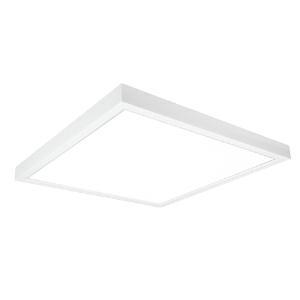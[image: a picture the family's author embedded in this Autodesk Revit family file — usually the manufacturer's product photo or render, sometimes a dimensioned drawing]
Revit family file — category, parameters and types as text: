
# Revit family: 3f_filippi_-_p_250_luce_diffusa_op_3f_filippi_-_10053_-_p_250_28w_led_dali_op_596x596
name_source: partatom
category: Lighting Fixtures
units: mm (PartAtom-declared; Revit-internal decimal feet)

## family parameters
Cut with Voids When Loaded = No
Host = Face
Light Source = No
Part Type = Normal
Room Calculation Point = No
Round Connector Dimension = Use Diameter
Shared = No

## types (1)
- 3F Filippi - P 250 Luce Diffusa OP (1 x LED, 4083 lm, 31 W, 4000 K)
    Apparent Load = 31 VA
    Approval mark = ENEC
    CIE Flux Codes = 48 80 96 100 100
    Color Rendering = 80
    Color Temperature = 4000 K
    Control Gear = Electronic transformer
    Default Elevation = 1800 mm
    Description = ILLUMINOTECHNICAL
Luminous efficiency 100% (DLOR 100%, ULOR 0%).
Initial luminous flux of the luminaire 4083 lm.
Direct distribution with soft, diffused and controlled light.
Installation Interdistance Transv.D = 1.24 x hu - Long.D = 1.21 x hu.
Tabular UGR (CIE 117 - 4H-8H; S=0.25H; 70/50/20): RUG 21.6 - 21.6.
Beam angle: 111° - 109°.
Luminous efficacy 132 lm/W.
Lifetime (L93/B10): 30000 h. (tq+25°C)
Lifetime (L90/B10): 50000 h. (tq+25°C)
Lifetime (L85/B10): 80000 h. (tq+25°C)
Lifetime (L80/B10): 100000 h. (tq+25°C)
Sudden decreased luminous flux after 50000 hours: 0% (C0).
Photobiological safety in compliance with IEC/TR 62778: RG0 risk exempt, (IEC 62471).
In compliance with IEC/EN 62722-2-1 - IEC/EN 62717 standards.

SOURCE
Squared LED module 28W/840.
Energy efficiency class (UE 2019/2020 - UE 2019/2015): D.
CIE 13.3 Colour rendering index: CRI >80 (R9 <50%).
IES TM-30 Fidelity Index: Rf = 84 Rg = 95.
CCT nominal colour temperature 4000 K.
Colour initial tolerance (MacAdam): SDCM 3.

MECHANICAL
Housing in galvannealed steel, painted in white epoxy-polyester.
Height only 55 mm.
OP opal methacrylate (PMMA) flat diffuser, anti-glare, locked to the pre-painted white aluminium perimeter frame, hinged opening.
Luminaire with limited surface temperature. - D - (EN 60598-2-24)
Dimensions: 596x596 mm, height 55 mm. Weight 5.085 kg.
IP40 protection degree.
Mechanical strength to impacts IK06 (1 joule).
Glow-wire test resistance 650°C.

ELECTRICAL
Halogen Free DALI-2 DATI (Parts 251, 252, 253), PUSH-DIM, electronic wiring 230V-50/60Hz, power factor 0.95 at full load, THD <25%, constant output current, SELV, class I, 1 driver, 1 DALI addresse.
Power of the luminaire 31 W.
CE - IEC 60598-1 - EN 60598-1.
SAFE FLICKER: PstLM=<1 and SVM=<0.4 (IEC TR 61547-1 and IEC TR 63158), to ensure a more comfortable and safe light.
Luminaire compliant with EN 60598-2-22 for power supply from a centralised emergency system CPSS (Central Power Supply System), not incorporated in the luminaire - high risk areas excluded. The default power and flux are 100% in AC and 15% in DC.
Ambient temperature from 0°C to +25°C.
Temperature class T6 max 85°C.
Relative humidity UR: <85%.

INSTALLATION
Ceiling.
All accessories dedicated to this product are available on the Catalog and on our website www.3F-Filippi.com.

APPLICATIONS
Particularly suitable for low height environments.
Environments where soft diffuse light is required for optimal visual comfort and total shielding of the source.

LIGHT MANAGEMENT
Recommended minimum setting: 10%.
The luminaire, equipped with (DALI-2 DATI) driver, can be controlled manually with 3F Easy Dim technology or automatically/manually with wired or wireless DALI/D2D control systems.
The D2D driver guarantees interoperability with other devices with the same certification by making the following information available:
Device Data (Part 251), Energy Report (Part 252), Diagnosis & Maintenance (Part 253).
In electrical systems without a regulation system (manual or automatic) and DALI bus, a suitable jumper must be made on the DA-DA terminals of the appliance.

WARNING
Luminaire designed for disposal/recycling at end-of-life.
Replaceable (LED only) light source by a professional. Replaceable control gear by a professional.
    Height = 55 mm
    Lamp = 1 x LED
    Lamp Light Flux = 4083 lm
    Lamp Power = 31 W
    Lamp count = 1
    Length = 596 mm
    Lifetime = 50000 h
    Luminous efficacy = 132 lm/W
    Manufacturer = 3F Filippi
    ModVariant = No
    Model = 3F Filippi - 10053 - P 250 28W LED DALI OP 596x596
    Mounting Place = Ceiling
    Mounting Type = Surface mounted
    Number of Poles = 1
    OnlyDefault = Yes
    Power Factor = 1
    Product Name = 3F Filippi - P 250 Luce Diffusa OP
    Product group = ceiling mounted luminaire
    ProductGroupID = 3
    Protection Class = Protection class I
    Protection Degree = IP 40
    RLX_Detail_Level = 1
    RLX_Emergency_Light_Flux = 0 lm
    RLX_Emergency_Type = 0
    RLX_Emergency_Type_DB = No
    RlxData = <blob elided: 32097 chars, md5=919089ee>
    Socket = socket
    Standby Power = 0 W
    System Light Flux = 4083 lm
    System Power = 31 W
    Type Comments = Product without accessories
    Type Image = 3ffilippi_p_250_led_luce_diffusa_opale.jpg
    URL = http://relux.com
    VarID = ---
    Voltage = 0 V
    Weight = 0.00 kg
    Width = 596 mm

## geometry (parser evidence)
native form markers: Blend x4, Sweep x9
no freeform markers — native parametric forms only
